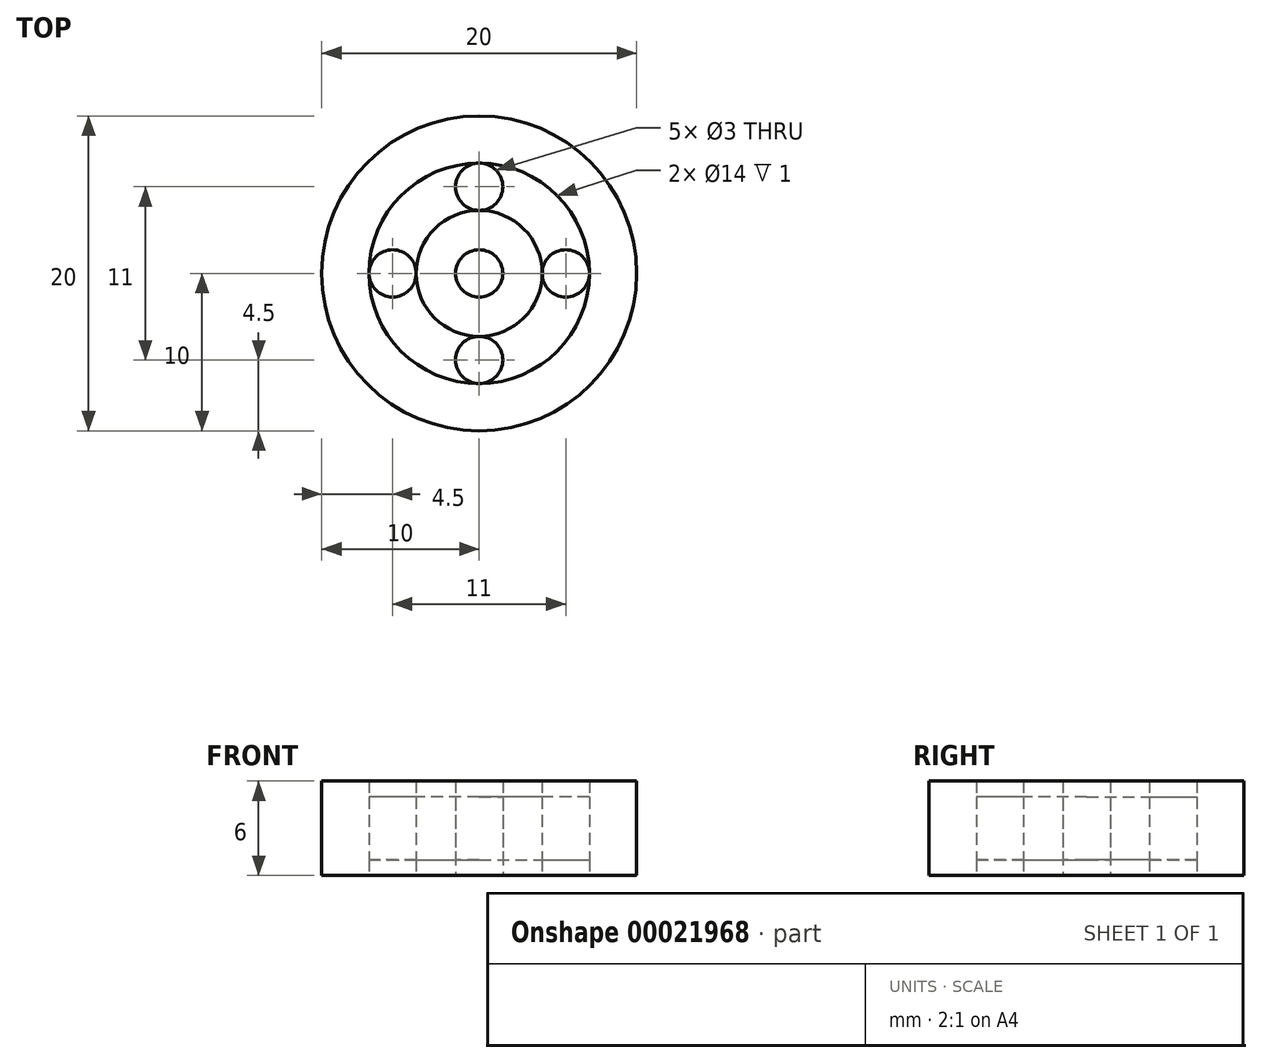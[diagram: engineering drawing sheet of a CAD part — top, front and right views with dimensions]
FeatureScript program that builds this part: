
annotation { "Feature Type Name" : "Feature", "Feature Type Description" : "" }
export const myFeature = defineFeature(function(context is Context, id is Id, definition is map)
    precondition{}
    {
        {
            var Q0;
            Q0=qCreatedBy(makeId("Top.planeOp"),FACE);
            var sketch = newSketch(context, id + "F0", { "sketchPlane" : qUnion([Q0])});
            skCircle(sketch, "E0", {"center": v(0, 0) * mm, "radius": 10 * mm});
            skCircle(sketch, "E1", {"center": v(0, 0) * mm, "radius": 7 * mm});
            skCircle(sketch, "E2", {"center": v(0, 0) * mm, "radius": 4 * mm});
            skCircle(sketch, "E3", {"center": v(0, 0) * mm, "radius": 1.5 * mm});
            skCircle(sketch, "E4", {"center": v(0, 5.5) * mm, "radius": 1.5 * mm});
            skCircle(sketch, "E5.1.0", {"center": v(-5.5, 0) * mm, "radius": 1.5 * mm});
            skCircle(sketch, "E5.2.0", {"center": v(0, -5.5) * mm, "radius": 1.5 * mm});
            skCircle(sketch, "E5.3.0", {"center": v(5.5, 0) * mm, "radius": 1.5 * mm});
            skSolve(sketch);
        }
        {
            var Q0;
            Q0=makeQuery(id+"F0.imprint","IMPRINT",FACE,{"disambiguationData":[TD([[makeQuery(id+"F0.imprint","IMPRINT",EDGE,{"derivedFrom":sQuery(id+"F0.wireOp",EDGE,"E3")}),-1.0]])]});
            var Q1;
            Q1=makeQuery(id+"F0.imprint","IMPRINT",FACE,{"disambiguationData":[TD([[makeQuery(id+"F0.imprint","IMPRINT",EDGE,{"derivedFrom":sQuery(id+"F0.wireOp",EDGE,"E0")}),1.0]])]});
            extrude(context, id + "F1", {"entities" : qUnion([Q0, Q1]), "endBound" : BoundingType.SYMMETRIC, "depth" : 6 * mm});
        }
        {
            var Q0;
            {var subQ3=sQuery(id+"F0.wireOp",EDGE,"E1");var subQ5=sQuery(id+"F0.wireOp",EDGE,"E4");var subQ7=makeQuery(id+"F0.imprint","INTERSECT",VERTEX,{"derivedFrom":[subQ3,subQ5]});Q0=makeQuery(id+"F0.imprint","IMPRINT",FACE,{"disambiguationData":[TD([[makeQuery(id+"F0.imprint","IMPRINT",EDGE,{"disambiguationData":[TD([[subQ7,-1.0]])],"derivedFrom":subQ3}),1.0]])]});}
            var Q1;
            {var subQ3=sQuery(id+"F0.wireOp",EDGE,"E1");var subQ5=sQuery(id+"F0.wireOp",EDGE,"E4");var subQ7=makeQuery(id+"F0.imprint","INTERSECT",VERTEX,{"derivedFrom":[subQ3,subQ5]});Q1=makeQuery(id+"F0.imprint","IMPRINT",FACE,{"disambiguationData":[TD([[makeQuery(id+"F0.imprint","IMPRINT",EDGE,{"disambiguationData":[TD([[subQ7,1.0]])],"derivedFrom":subQ3}),1.0]])]});}
            var Q2;
            {var subQ0=sQuery(id+"F0.wireOp",EDGE,"E5.3.0");var subQ3=sQuery(id+"F0.wireOp",EDGE,"E1");var subQ4=makeQuery(id+"F0.imprint","INTERSECT",VERTEX,{"derivedFrom":[subQ3,subQ0]});Q2=makeQuery(id+"F0.imprint","IMPRINT",FACE,{"disambiguationData":[TD([[makeQuery(id+"F0.imprint","IMPRINT",EDGE,{"disambiguationData":[TD([[subQ4,1.0]])],"derivedFrom":subQ3}),1.0]])]});}
            var Q3;
            {var subQ3=sQuery(id+"F0.wireOp",EDGE,"E1");var subQ5=sQuery(id+"F0.wireOp",EDGE,"E5.1.0");var subQ7=makeQuery(id+"F0.imprint","INTERSECT",VERTEX,{"derivedFrom":[subQ3,subQ5]});Q3=makeQuery(id+"F0.imprint","IMPRINT",FACE,{"disambiguationData":[TD([[makeQuery(id+"F0.imprint","IMPRINT",EDGE,{"disambiguationData":[TD([[subQ7,-1.0]])],"derivedFrom":subQ3}),1.0]])]});}
            extrude(context, id + "F2", {"entities" : qUnion([Q0, Q1, Q2, Q3]), "operationType" : NewBodyOperationType.ADD, "endBound" : BoundingType.SYMMETRIC, "depth" : 4 * mm});
        }
    });
